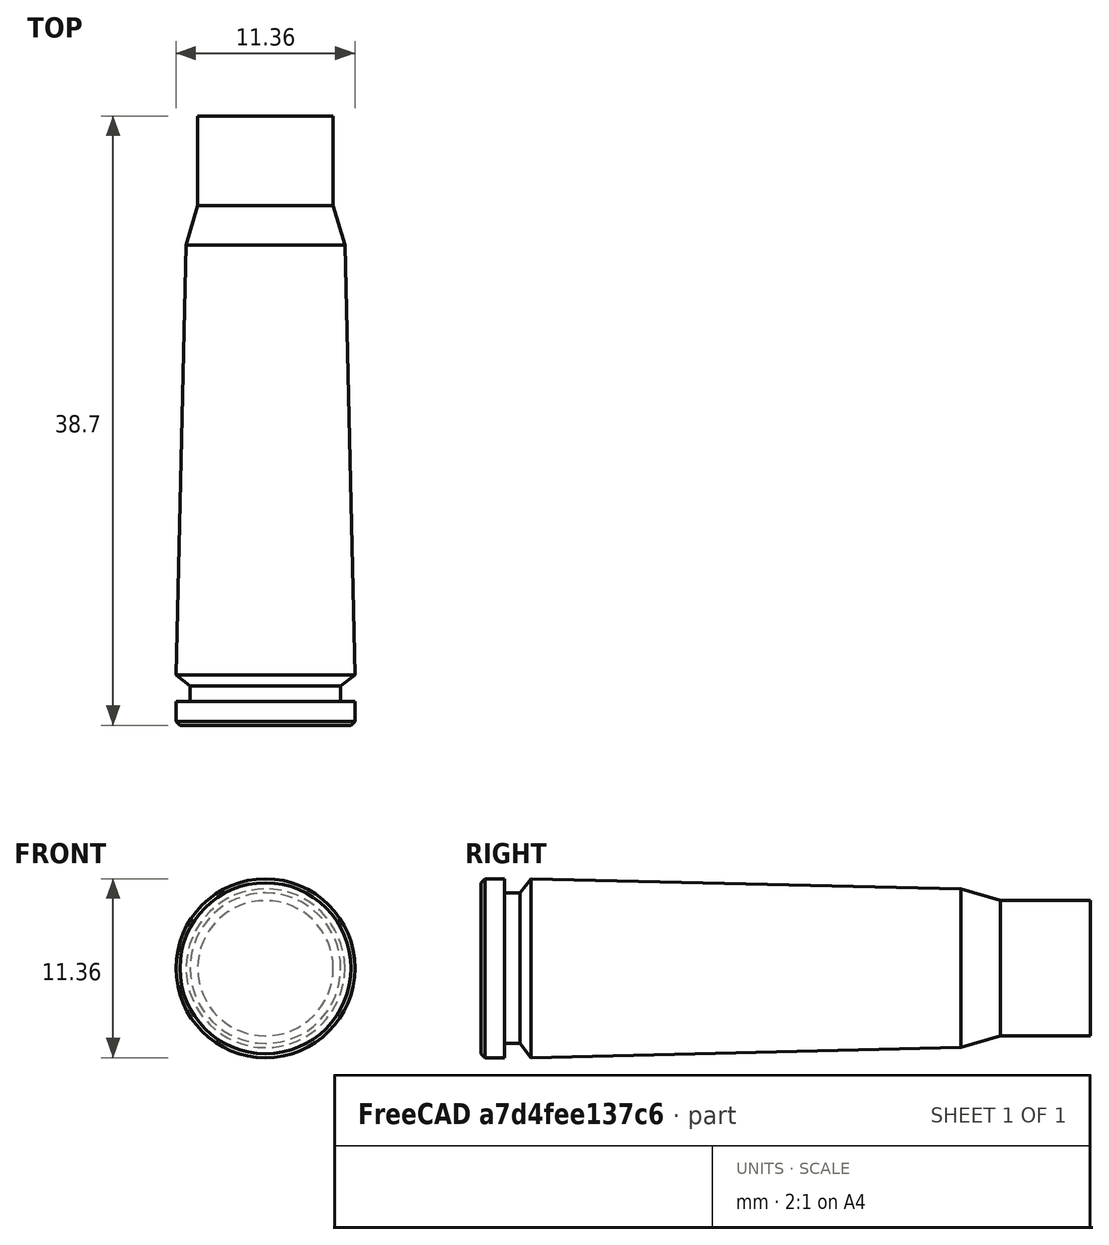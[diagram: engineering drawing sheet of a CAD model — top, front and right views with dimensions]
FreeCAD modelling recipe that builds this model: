
FCSTD DOCUMENT
Label: 762x39
objects: Sketcher::SketchObject×1, PartDesign::Revolution×1
note: 2 computed .brp shape members not serialized (recipe doc carries the construction recipe); baked Part::Feature solids carry a one-line shape summary decoded from their .brp

FEATURE [Sketcher::SketchObject] Sketch
  sketch-geometry (11):
    g0: LineSegment StartX=0 StartY=0 StartZ=0 EndX=5.43 EndY=0 EndZ=0
    g1: LineSegment StartX=5.43 StartY=0 StartZ=0 EndX=5.68 EndY=0.25 EndZ=0
    g2: LineSegment StartX=5.68 StartY=0.25 StartZ=0 EndX=5.68 EndY=1.5 EndZ=0
    g3: LineSegment StartX=5.68 StartY=1.5 StartZ=0 EndX=4.78 EndY=1.5 EndZ=0
    g4: LineSegment StartX=4.78 StartY=1.5 StartZ=0 EndX=4.78 EndY=2.5 EndZ=0
    g5: LineSegment StartX=4.78 StartY=2.5 StartZ=0 EndX=5.68 EndY=3.2 EndZ=0
    g6: LineSegment StartX=5.68 StartY=3.2 StartZ=0 EndX=5.04 EndY=30.5 EndZ=0
    g7: LineSegment StartX=5.04 StartY=30.5 StartZ=0 EndX=4.3 EndY=33 EndZ=0
    g8: LineSegment StartX=4.3 StartY=33 StartZ=0 EndX=4.3 EndY=38.7 EndZ=0
    g9: LineSegment StartX=4.3 StartY=38.7 StartZ=0 EndX=0 EndY=38.7 EndZ=0
    g10: LineSegment StartX=0 StartY=38.7 StartZ=0 EndX=0 EndY=0 EndZ=0
  constraints (33):
    c: Horizontal(g0)
    c: Coincident(g0,g1)
    c: Coincident(g1,g2)
    c: Vertical(g2)
    c: Coincident(g2,g3)
    c: Horizontal(g3)
    c: Coincident(g3,g4)
    c: Vertical(g4)
    c: Coincident(g4,g5)
    c: Coincident(g5,g6)
    c: Coincident(g6,g7)
    c: Coincident(g7,g8)
    c: Vertical(g8)
    c: Coincident(g8,g9)
    c: Horizontal(g9)
    c: Coincident(g9,g10)
    c: Vertical(g10)
    c: Coincident(g10,g0)
    c: DistanceX(g1,g0) = -5.68
    c: Angle(g1) = 0.785398
    c: DistanceX(g3,g0) = -4.78
    c: DistanceX(g5,g0) = -5.68
    c: DistanceX(g6,g0) = -5.04
    c: DistanceX(g7,g0) = -4.3
    c: DistanceY(g0,g1) = 0.25
    c: DistanceY(g2,g0) = -1.5
    c: DistanceY(g3,g4) = 1
    c: DistanceY(g5,g0) = -3.2
    c: DistanceY(g0,g6) = 30.5
    c: DistanceY(g0,g7) = 33
    c: DistanceY(g8,g0) = -38.7
    c: DistanceX(g0) = 0
    c: DistanceY(g0) = 0
FEATURE [PartDesign::Revolution] Revolution
  Angle = 360
  Axis = (0,1,0)
  Base = (0,0,0)
  Sketch = -> Sketch
